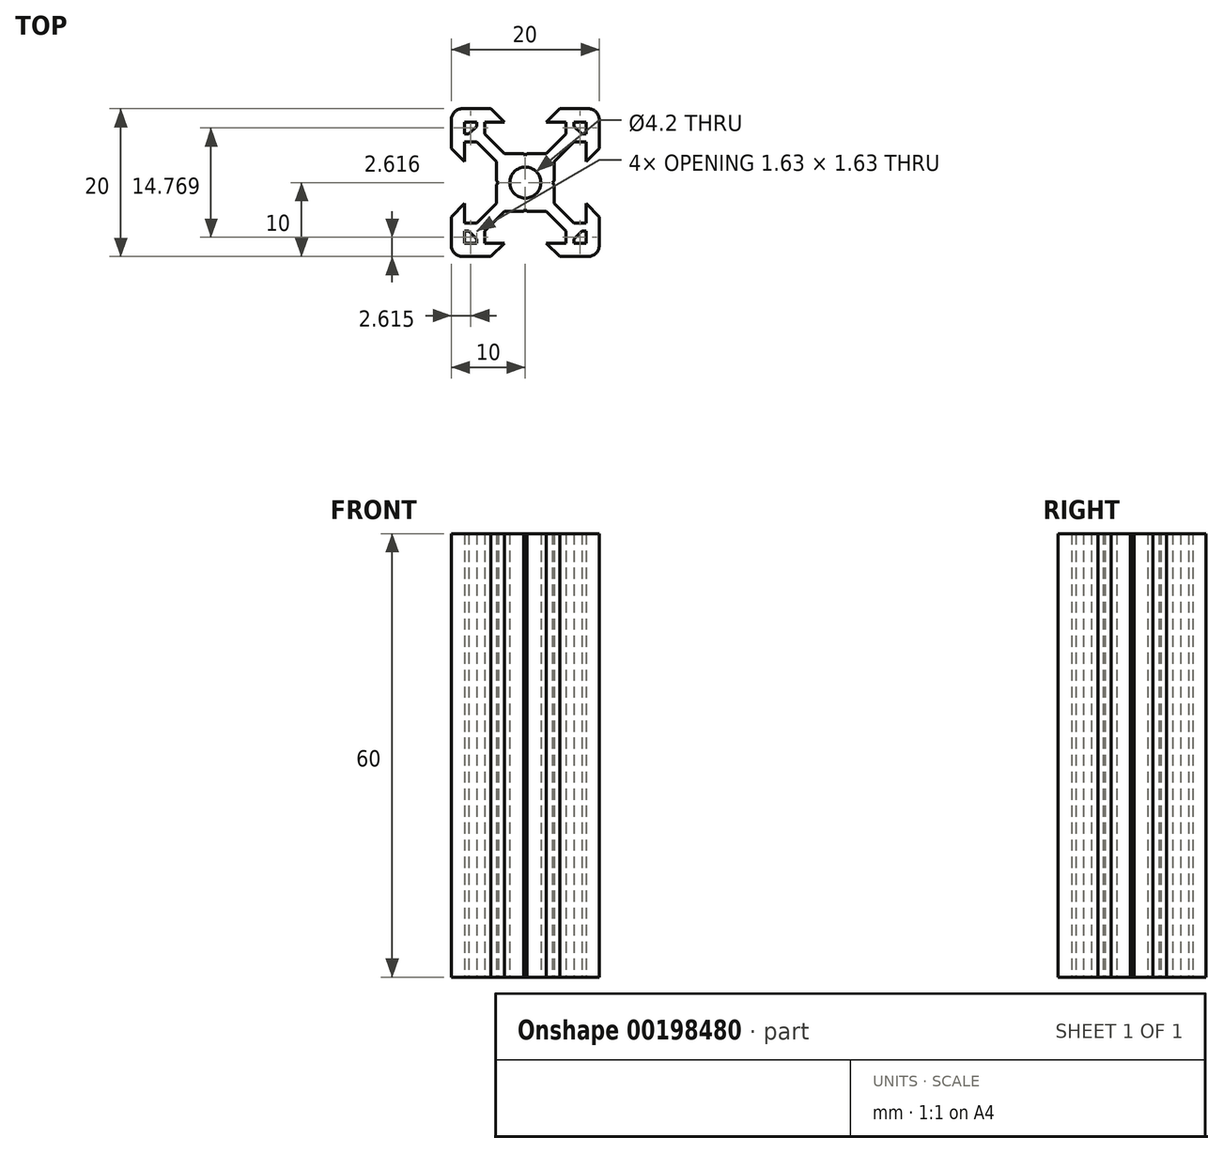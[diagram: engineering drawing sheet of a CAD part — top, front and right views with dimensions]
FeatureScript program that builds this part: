
annotation { "Feature Type Name" : "Feature", "Feature Type Description" : "" }
export const myFeature = defineFeature(function(context is Context, id is Id, definition is map)
    precondition{}
    {
        {
            var Q0;
            Q0=qCreatedBy(makeId("Top.planeOp"),FACE);
            var sketch = newSketch(context, id + "F0", { "sketchPlane" : qUnion([Q0])});
            skLineSegment(sketch, "E0", {"start": v(10, 8.27) * mm, "end": v(10, 4.41) * mm});
            skLineSegment(sketch, "E1", {"start": v(8.5, -10.23) * mm, "end": v(4.64, -10.23) * mm});
            skLineSegment(sketch, "E2", {"start": v(-10, -8.73) * mm, "end": v(-10, -4.87) * mm});
            skLineSegment(sketch, "E3", {"start": v(-8.5, 9.77) * mm, "end": v(-4.64, 9.77) * mm});
            skLineSegment(sketch, "E4.0", {"start": v(-5.5, 7.97) * mm, "end": v(-2.84, 7.97) * mm});
            skLineSegment(sketch, "E4.1", {"start": v(-8.2, -5.73) * mm, "end": v(-8.2, -3.07) * mm});
            skLineSegment(sketch, "E4.2", {"start": v(5.5, -8.43) * mm, "end": v(2.84, -8.43) * mm});
            skLineSegment(sketch, "E4.3", {"start": v(8.2, 5.27) * mm, "end": v(8.2, 2.61) * mm});
            skLineSegment(sketch, "E5.trimOffspring", {"start": v(4.64, 9.77) * mm, "end": v(8.5, 9.77) * mm});
            skPoint(sketch, "E6.start.orphan", {"position": v(0, 9.77) * mm});
            skLineSegment(sketch, "E7", {"start": v(-2.84, 7.97) * mm, "end": v(-4.64, 9.77) * mm});
            skLineSegment(sketch, "E8.trimOffspring", {"start": v(2.84, 7.97) * mm, "end": v(5.5, 7.97) * mm});
            skLineSegment(sketch, "E9.MirrorCS", {"start": v(2.84, 7.97) * mm, "end": v(4.64, 9.77) * mm});
            skLineSegment(sketch, "E10.MirrorCS", {"start": v(2.84, -8.43) * mm, "end": v(4.64, -10.23) * mm});
            skLineSegment(sketch, "E11.MirrorCS", {"start": v(-2.84, -8.43) * mm, "end": v(-4.64, -10.23) * mm});
            skLineSegment(sketch, "E12.trimOffspring", {"start": v(-2.84, -8.43) * mm, "end": v(-5.5, -8.43) * mm});
            skLineSegment(sketch, "E13.trimOffspring", {"start": v(-4.64, -10.23) * mm, "end": v(-8.5, -10.23) * mm});
            skLineSegment(sketch, "E14", {"start": v(-8.2, 2.61) * mm, "end": v(-10, 4.41) * mm});
            skLineSegment(sketch, "E15", {"start": v(-8.2, -3.07) * mm, "end": v(-10, -4.87) * mm});
            skLineSegment(sketch, "E16.trimOffspring", {"start": v(-10, 4.41) * mm, "end": v(-10, 8.27) * mm});
            skLineSegment(sketch, "E17.trimOffspring", {"start": v(-8.2, 2.61) * mm, "end": v(-8.2, 5.27) * mm});
            skLineSegment(sketch, "E18.MirrorCS", {"start": v(8.2, 2.61) * mm, "end": v(10, 4.41) * mm});
            skLineSegment(sketch, "E19.MirrorCS", {"start": v(8.2, -3.07) * mm, "end": v(10, -4.87) * mm});
            skLineSegment(sketch, "E20.trimOffspring", {"start": v(8.2, -3.07) * mm, "end": v(8.2, -5.73) * mm});
            skLineSegment(sketch, "E21.trimOffspring", {"start": v(10, -4.87) * mm, "end": v(10, -8.73) * mm});
            skCircle(sketch, "E22", {"center": v(0, -0.23) * mm, "radius": 2.1 * mm});
            skLineSegment(sketch, "E23", {"start": v(-6.56, 5.27) * mm, "end": v(-3.9, 2.61) * mm});
            skLineSegment(sketch, "E24", {"start": v(-5.5, 6.33) * mm, "end": v(-2.84, 3.67) * mm});
            skLineSegment(sketch, "E25", {"start": v(-5.5, 6.33) * mm, "end": v(-5.5, 7.97) * mm});
            skLineSegment(sketch, "E26", {"start": v(-6.56, 5.27) * mm, "end": v(-8.2, 5.27) * mm});
            skLineSegment(sketch, "E27", {"start": v(6.56, 5.27) * mm, "end": v(3.9, 2.61) * mm});
            skLineSegment(sketch, "E28", {"start": v(5.5, 6.33) * mm, "end": v(2.84, 3.67) * mm});
            skLineSegment(sketch, "E29", {"start": v(-6.56, -5.73) * mm, "end": v(-8.2, -5.73) * mm});
            skLineSegment(sketch, "E30", {"start": v(-5.5, -6.79) * mm, "end": v(-5.5, -8.43) * mm});
            skLineSegment(sketch, "E31", {"start": v(5.5, 6.33) * mm, "end": v(5.5, 7.97) * mm});
            skLineSegment(sketch, "E32", {"start": v(6.56, 5.27) * mm, "end": v(8.2, 5.27) * mm});
            skLineSegment(sketch, "E33", {"start": v(5.5, -6.79) * mm, "end": v(5.5, -8.43) * mm});
            skLineSegment(sketch, "E34", {"start": v(6.56, -5.73) * mm, "end": v(8.2, -5.73) * mm});
            skLineSegment(sketch, "E35.trimOffspring", {"start": v(2.84, -4.13) * mm, "end": v(5.5, -6.79) * mm});
            skLineSegment(sketch, "E36.trimOffspring", {"start": v(-2.84, -4.13) * mm, "end": v(-5.5, -6.79) * mm});
            skLineSegment(sketch, "E37.trimOffspring", {"start": v(-3.9, -3.07) * mm, "end": v(-6.56, -5.73) * mm});
            skLineSegment(sketch, "E38.trimOffspring", {"start": v(3.9, -3.07) * mm, "end": v(6.56, -5.73) * mm});
            skLineSegment(sketch, "E39", {"start": v(-3.9, -3.07) * mm, "end": v(-3.9, -0.48) * mm});
            skLineSegment(sketch, "E40", {"start": v(-2.84, 3.67) * mm, "end": v(-0.25, 3.67) * mm});
            skLineSegment(sketch, "E41", {"start": v(-2.84, -4.13) * mm, "end": v(-0.25, -4.13) * mm});
            skLineSegment(sketch, "E42", {"start": v(3.9, 2.61) * mm, "end": v(3.9, 0.02) * mm});
            skLineSegment(sketch, "E43", {"start": v(-8.2, 6.34) * mm, "end": v(-8.2, 7.97) * mm});
            skLineSegment(sketch, "E44", {"start": v(-6.57, 7.97) * mm, "end": v(-8.2, 7.97) * mm});
            skLineSegment(sketch, "E45", {"start": v(-8.2, 6.34) * mm, "end": v(-7.63, 6.34) * mm});
            skLineSegment(sketch, "E46", {"start": v(-6.57, 7.97) * mm, "end": v(-6.57, 7.4) * mm});
            skLineSegment(sketch, "E47", {"start": v(-7.63, 6.34) * mm, "end": v(-6.57, 7.4) * mm});
            skLineSegment(sketch, "E48.MirrorCS", {"start": v(6.57, 7.97) * mm, "end": v(8.2, 7.97) * mm});
            skLineSegment(sketch, "E49.MirrorCS", {"start": v(8.2, 6.34) * mm, "end": v(8.2, 7.97) * mm});
            skLineSegment(sketch, "E50.MirrorCS", {"start": v(8.2, 6.34) * mm, "end": v(7.63, 6.34) * mm});
            skLineSegment(sketch, "E51.MirrorCS", {"start": v(7.63, 6.34) * mm, "end": v(6.57, 7.4) * mm});
            skLineSegment(sketch, "E52.MirrorCS", {"start": v(6.57, 7.97) * mm, "end": v(6.57, 7.4) * mm});
            skLineSegment(sketch, "E53.MirrorCS", {"start": v(6.57, -8.43) * mm, "end": v(6.57, -7.86) * mm});
            skLineSegment(sketch, "E54.MirrorCS", {"start": v(8.2, -6.8) * mm, "end": v(7.63, -6.8) * mm});
            skLineSegment(sketch, "E55.MirrorCS", {"start": v(7.63, -6.8) * mm, "end": v(6.57, -7.86) * mm});
            skLineSegment(sketch, "E56.MirrorCS", {"start": v(6.57, -8.43) * mm, "end": v(8.2, -8.43) * mm});
            skLineSegment(sketch, "E57.MirrorCS", {"start": v(8.2, -6.8) * mm, "end": v(8.2, -8.43) * mm});
            skLineSegment(sketch, "E58.MirrorCS", {"start": v(-6.57, -8.43) * mm, "end": v(-8.2, -8.43) * mm});
            skLineSegment(sketch, "E59.MirrorCS", {"start": v(-8.2, -6.8) * mm, "end": v(-7.63, -6.8) * mm});
            skLineSegment(sketch, "E60.MirrorCS", {"start": v(-8.2, -6.8) * mm, "end": v(-8.2, -8.43) * mm});
            skLineSegment(sketch, "E61.MirrorCS", {"start": v(-7.63, -6.8) * mm, "end": v(-6.57, -7.86) * mm});
            skLineSegment(sketch, "E62.MirrorCS", {"start": v(-6.57, -8.43) * mm, "end": v(-6.57, -7.86) * mm});
            skPoint(sketch, "E63.visualSharp", {"position": v(-10, 9.77) * mm});
            skArc(sketch, "E63.filletArc", {"start": v(-8.5, 9.77) * mm, "mid": v(-9.56, 9.33) * mm, "end": v(-10, 8.27) * mm});
            skPoint(sketch, "E64.visualSharp", {"position": v(10, 9.77) * mm});
            skArc(sketch, "E64.filletArc", {"start": v(10, 8.27) * mm, "mid": v(9.56, 9.33) * mm, "end": v(8.5, 9.77) * mm});
            skPoint(sketch, "E65.visualSharp", {"position": v(10, -10.23) * mm});
            skArc(sketch, "E65.filletArc", {"start": v(8.5, -10.23) * mm, "mid": v(9.56, -9.8) * mm, "end": v(10, -8.73) * mm});
            skPoint(sketch, "E66.visualSharp", {"position": v(-10, -10.23) * mm});
            skArc(sketch, "E66.filletArc", {"start": v(-10, -8.73) * mm, "mid": v(-9.56, -9.8) * mm, "end": v(-8.5, -10.23) * mm});
            skLineSegment(sketch, "E67", {"start": v(-3.65, -0.23) * mm, "end": v(-3.9, 0.02) * mm});
            skLineSegment(sketch, "E68.MirrorCS", {"start": v(-3.65, -0.23) * mm, "end": v(-3.9, -0.48) * mm});
            skLineSegment(sketch, "E69.trimOffspring", {"start": v(-3.9, 0.02) * mm, "end": v(-3.9, 2.61) * mm});
            skLineSegment(sketch, "E70.MirrorCS", {"start": v(3.65, -0.23) * mm, "end": v(3.9, 0.02) * mm});
            skLineSegment(sketch, "E71.MirrorCS", {"start": v(3.65, -0.23) * mm, "end": v(3.9, -0.48) * mm});
            skLineSegment(sketch, "E72", {"start": v(0, -3.88) * mm, "end": v(0.25, -4.13) * mm});
            skLineSegment(sketch, "E73.MirrorCS", {"start": v(0, -3.88) * mm, "end": v(-0.25, -4.13) * mm});
            skLineSegment(sketch, "E74.trimOffspring", {"start": v(0.25, -4.13) * mm, "end": v(2.84, -4.13) * mm});
            skLineSegment(sketch, "E75.trimOffspring", {"start": v(3.9, -0.48) * mm, "end": v(3.9, -3.07) * mm});
            skLineSegment(sketch, "E76.MirrorCS", {"start": v(0, 3.42) * mm, "end": v(-0.25, 3.67) * mm});
            skLineSegment(sketch, "E77.MirrorCS", {"start": v(0, 3.42) * mm, "end": v(0.25, 3.67) * mm});
            skLineSegment(sketch, "E78.trimOffspring", {"start": v(0.25, 3.67) * mm, "end": v(2.84, 3.67) * mm});
            skSolve(sketch);
        }
        {
            var Q0;
            Q0 = qSketchRegion(id + "F0", true);
            extrude(context, id + "F1", {"entities" : qUnion([Q0]), "depth" : 60 * mm});
        }
    });
